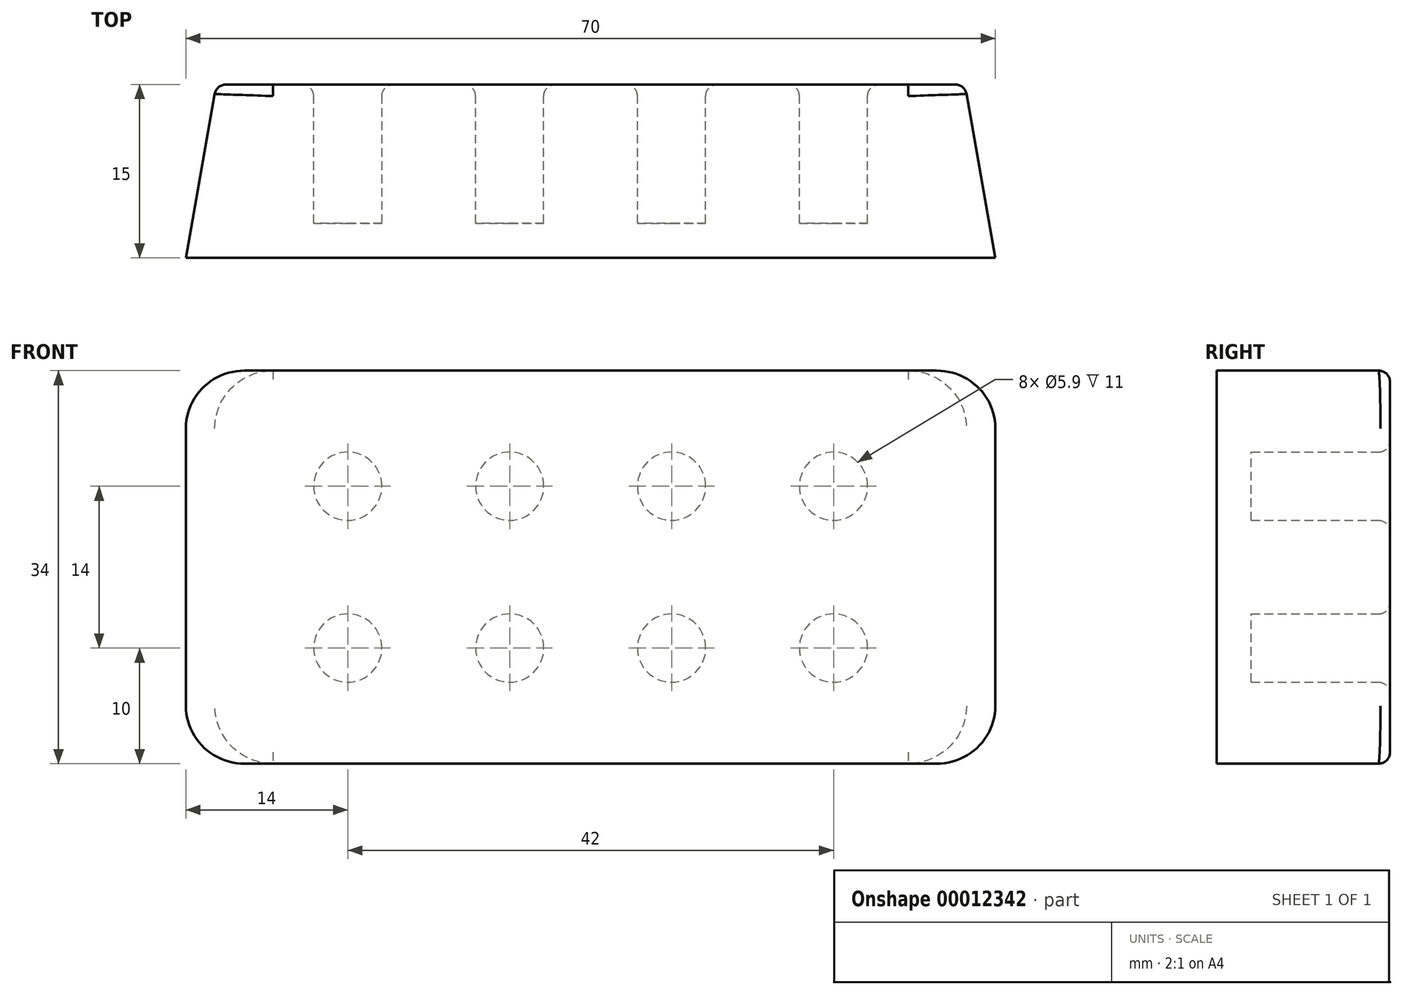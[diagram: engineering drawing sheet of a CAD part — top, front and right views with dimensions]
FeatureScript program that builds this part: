
annotation { "Feature Type Name" : "Feature", "Feature Type Description" : "" }
export const myFeature = defineFeature(function(context is Context, id is Id, definition is map)
    precondition{}
    {
        {
            var Q0;
            Q0=qCreatedBy(makeId("Front.planeOp"),FACE);
            var sketch = newSketch(context, id + "F0", { "sketchPlane" : qUnion([Q0])});
            skLineSegment(sketch, "E0.bottom", {"start": v(0, 0) * mm, "end": v(70, 0) * mm});
            skLineSegment(sketch, "E0.top", {"start": v(0, 34) * mm, "end": v(70, 34) * mm});
            skLineSegment(sketch, "E0.left", {"start": v(0, 0) * mm, "end": v(0, 34) * mm});
            skLineSegment(sketch, "E0.right", {"start": v(70, 0) * mm, "end": v(70, 34) * mm});
            skCircle(sketch, "E1", {"center": v(14, 10) * mm, "radius": 2.95 * mm});
            skCircle(sketch, "E2.0.1.0", {"center": v(14, 24) * mm, "radius": 2.95 * mm});
            skCircle(sketch, "E2.1.0.0", {"center": v(28, 10) * mm, "radius": 2.95 * mm});
            skCircle(sketch, "E2.1.1.0", {"center": v(28, 24) * mm, "radius": 2.95 * mm});
            skCircle(sketch, "E2.2.0.0", {"center": v(42, 10) * mm, "radius": 2.95 * mm});
            skCircle(sketch, "E2.2.1.0", {"center": v(42, 24) * mm, "radius": 2.95 * mm});
            skCircle(sketch, "E2.3.0.0", {"center": v(56, 10) * mm, "radius": 2.95 * mm});
            skCircle(sketch, "E2.3.1.0", {"center": v(56, 24) * mm, "radius": 2.95 * mm});
            skLineSegment(sketch, "E2.direction1", {"start": v(14, 10) * mm, "end": v(28, 10) * mm, "construction": true});
            skLineSegment(sketch, "E2.direction2", {"start": v(14, 10) * mm, "end": v(14, 24) * mm, "construction": true});
            skSolve(sketch);
        }
        {
            var Q0;
            Q0=makeQuery(id+"F0.imprint","IMPRINT",FACE,{"disambiguationData":[TD([[makeQuery(id+"F0.imprint","IMPRINT",EDGE,{"derivedFrom":sQuery(id+"F0.wireOp",EDGE,"E0.bottom")}),1.0]])]});
            extrude(context, id + "F1", {"entities" : qUnion([Q0]), "depth" : 12 * mm});
        }
        {
            var Q0;
            Q0=makeQuery(id+"F1.opExtrude","CAP_FACE",FACE,{"disambiguationData":[OSD([sQuery(id+"F0.wireOp",EDGE,"E0.bottom"),sQuery(id+"F0.wireOp",EDGE,"E0.top"),sQuery(id+"F0.wireOp",EDGE,"E0.left"),sQuery(id+"F0.wireOp",EDGE,"E0.right"),sQuery(id+"F0.wireOp",EDGE,"E1"),sQuery(id+"F0.wireOp",EDGE,"E2.0.1.0"),sQuery(id+"F0.wireOp",EDGE,"E2.1.0.0"),sQuery(id+"F0.wireOp",EDGE,"E2.1.1.0"),sQuery(id+"F0.wireOp",EDGE,"E2.2.0.0"),sQuery(id+"F0.wireOp",EDGE,"E2.2.1.0"),sQuery(id+"F0.wireOp",EDGE,"E2.3.0.0"),sQuery(id+"F0.wireOp",EDGE,"E2.3.1.0")])],"isStart":false});
            var sketch = newSketch(context, id + "F2", { "sketchPlane" : qUnion([Q0])});
            skLineSegment(sketch, "E3.bottom", {"start": v(0, 34) * mm, "end": v(70, 34) * mm});
            skLineSegment(sketch, "E3.top", {"start": v(0, 0) * mm, "end": v(70, 0) * mm});
            skLineSegment(sketch, "E3.left", {"start": v(0, 34) * mm, "end": v(0, 0) * mm});
            skLineSegment(sketch, "E3.right", {"start": v(70, 34) * mm, "end": v(70, 0) * mm});
            skSolve(sketch);
        }
        {
            var Q0;
            Q0 = qSketchRegion(id + "F2", true);
            extrude(context, id + "F3", {"entities" : qUnion([Q0]), "operationType" : NewBodyOperationType.ADD, "depth" : 3 * mm});
        }
        {
            var Q0;
            Q0=makeQuery(id+"F1.opExtrude","CAP_EDGE",EDGE,{"disambiguationData":[OSD([sQuery(id+"F0.wireOp",EDGE,"E0.left")])],"isStart":true});
            var Q1;
            Q1=makeQuery(id+"F1.opExtrude","CAP_EDGE",EDGE,{"disambiguationData":[OSD([sQuery(id+"F0.wireOp",EDGE,"E0.right")])],"isStart":true});
            chamfer(context, id + "F4", {"entities" : qUnion([Q0, Q1]), "chamferType" : ChamferType.OFFSET_ANGLE, "width" : 15 * mm, "oppositeDirection" : true, "angle" : 10 * degree});
        }
        {
            var Q0;
            Q0=makeQuery(id+"F4.opChamfer","BLEND_EDGE",EDGE,{"blendedFrom":[makeQuery(id+"F1.opExtrude","CAP_EDGE",EDGE,{"disambiguationData":[OSD([sQuery(id+"F0.wireOp",EDGE,"E0.left")])],"isStart":true}),makeQuery(id+"F3.boolean.opBoolean","MERGE",FACE,{"derivedFrom":[makeQuery(id+"F1.opExtrude","SWEPT_FACE",FACE,{"disambiguationData":[OSD([sQuery(id+"F0.wireOp",EDGE,"E0.bottom")])]}),makeQuery(id+"F3.opExtrude","SWEPT_FACE",FACE,{"disambiguationData":[OSD([sQuery(id+"F2.wireOp",EDGE,"E3.top")])]})]})],"blendedInto":[makeQuery(id+"F3.boolean.opBoolean","MERGE",FACE,{"derivedFrom":[makeQuery(id+"F1.opExtrude","SWEPT_FACE",FACE,{"disambiguationData":[OSD([sQuery(id+"F0.wireOp",EDGE,"E0.bottom")])]}),makeQuery(id+"F3.opExtrude","SWEPT_FACE",FACE,{"disambiguationData":[OSD([sQuery(id+"F2.wireOp",EDGE,"E3.top")])]})]})]});
            var Q1;
            Q1=makeQuery(id+"F4.opChamfer","BLEND_EDGE",EDGE,{"blendedFrom":[makeQuery(id+"F1.opExtrude","CAP_EDGE",EDGE,{"disambiguationData":[OSD([sQuery(id+"F0.wireOp",EDGE,"E0.left")])],"isStart":true}),makeQuery(id+"F3.boolean.opBoolean","MERGE",FACE,{"derivedFrom":[makeQuery(id+"F1.opExtrude","SWEPT_FACE",FACE,{"disambiguationData":[OSD([sQuery(id+"F0.wireOp",EDGE,"E0.top")])]}),makeQuery(id+"F3.opExtrude","SWEPT_FACE",FACE,{"disambiguationData":[OSD([sQuery(id+"F2.wireOp",EDGE,"E3.bottom")])]})]})],"blendedInto":[makeQuery(id+"F3.boolean.opBoolean","MERGE",FACE,{"derivedFrom":[makeQuery(id+"F1.opExtrude","SWEPT_FACE",FACE,{"disambiguationData":[OSD([sQuery(id+"F0.wireOp",EDGE,"E0.top")])]}),makeQuery(id+"F3.opExtrude","SWEPT_FACE",FACE,{"disambiguationData":[OSD([sQuery(id+"F2.wireOp",EDGE,"E3.bottom")])]})]})]});
            var Q2;
            Q2=makeQuery(id+"F4.opChamfer","BLEND_EDGE",EDGE,{"blendedFrom":[makeQuery(id+"F1.opExtrude","CAP_EDGE",EDGE,{"disambiguationData":[OSD([sQuery(id+"F0.wireOp",EDGE,"E0.right")])],"isStart":true}),makeQuery(id+"F3.boolean.opBoolean","MERGE",FACE,{"derivedFrom":[makeQuery(id+"F1.opExtrude","SWEPT_FACE",FACE,{"disambiguationData":[OSD([sQuery(id+"F0.wireOp",EDGE,"E0.top")])]}),makeQuery(id+"F3.opExtrude","SWEPT_FACE",FACE,{"disambiguationData":[OSD([sQuery(id+"F2.wireOp",EDGE,"E3.bottom")])]})]})],"blendedInto":[makeQuery(id+"F3.boolean.opBoolean","MERGE",FACE,{"derivedFrom":[makeQuery(id+"F1.opExtrude","SWEPT_FACE",FACE,{"disambiguationData":[OSD([sQuery(id+"F0.wireOp",EDGE,"E0.top")])]}),makeQuery(id+"F3.opExtrude","SWEPT_FACE",FACE,{"disambiguationData":[OSD([sQuery(id+"F2.wireOp",EDGE,"E3.bottom")])]})]})]});
            var Q3;
            Q3=makeQuery(id+"F4.opChamfer","BLEND_EDGE",EDGE,{"blendedFrom":[makeQuery(id+"F1.opExtrude","CAP_EDGE",EDGE,{"disambiguationData":[OSD([sQuery(id+"F0.wireOp",EDGE,"E0.right")])],"isStart":true}),makeQuery(id+"F3.boolean.opBoolean","MERGE",FACE,{"derivedFrom":[makeQuery(id+"F1.opExtrude","SWEPT_FACE",FACE,{"disambiguationData":[OSD([sQuery(id+"F0.wireOp",EDGE,"E0.bottom")])]}),makeQuery(id+"F3.opExtrude","SWEPT_FACE",FACE,{"disambiguationData":[OSD([sQuery(id+"F2.wireOp",EDGE,"E3.top")])]})]})],"blendedInto":[makeQuery(id+"F3.boolean.opBoolean","MERGE",FACE,{"derivedFrom":[makeQuery(id+"F1.opExtrude","SWEPT_FACE",FACE,{"disambiguationData":[OSD([sQuery(id+"F0.wireOp",EDGE,"E0.bottom")])]}),makeQuery(id+"F3.opExtrude","SWEPT_FACE",FACE,{"disambiguationData":[OSD([sQuery(id+"F2.wireOp",EDGE,"E3.top")])]})]})]});
            fillet(context, id + "F5", {"entities" : qUnion([Q0, Q1, Q2, Q3]), "radius" : 5 * mm, "tangentPropagation" : true, "allowEdgeOverflow" : false});
        }
        {
            var Q0;
            Q0=makeQuery(id+"F1.opExtrude","CAP_EDGE",EDGE,{"disambiguationData":[OSD([sQuery(id+"F0.wireOp",EDGE,"E1")])],"isStart":true});
            var Q1;
            Q1=makeQuery(id+"F1.opExtrude","CAP_EDGE",EDGE,{"disambiguationData":[OSD([sQuery(id+"F0.wireOp",EDGE,"E2.1.0.0")])],"isStart":true});
            var Q2;
            Q2=makeQuery(id+"F1.opExtrude","CAP_EDGE",EDGE,{"disambiguationData":[OSD([sQuery(id+"F0.wireOp",EDGE,"E2.0.1.0")])],"isStart":true});
            var Q3;
            Q3=makeQuery(id+"F1.opExtrude","CAP_EDGE",EDGE,{"disambiguationData":[OSD([sQuery(id+"F0.wireOp",EDGE,"E2.1.1.0")])],"isStart":true});
            var Q4;
            Q4=makeQuery(id+"F1.opExtrude","CAP_EDGE",EDGE,{"disambiguationData":[OSD([sQuery(id+"F0.wireOp",EDGE,"E2.2.1.0")])],"isStart":true});
            var Q5;
            Q5=makeQuery(id+"F1.opExtrude","CAP_EDGE",EDGE,{"disambiguationData":[OSD([sQuery(id+"F0.wireOp",EDGE,"E2.2.0.0")])],"isStart":true});
            var Q6;
            Q6=makeQuery(id+"F1.opExtrude","CAP_EDGE",EDGE,{"disambiguationData":[OSD([sQuery(id+"F0.wireOp",EDGE,"E2.3.0.0")])],"isStart":true});
            var Q7;
            Q7=makeQuery(id+"F1.opExtrude","CAP_EDGE",EDGE,{"disambiguationData":[OSD([sQuery(id+"F0.wireOp",EDGE,"E2.3.1.0")])],"isStart":true});
            var Q8;
            Q8=makeQuery(id+"F1.opExtrude","CAP_EDGE",EDGE,{"disambiguationData":[OSD([sQuery(id+"F0.wireOp",EDGE,"E0.top")])],"isStart":true});
            fillet(context, id + "F6", {"entities" : qUnion([Q0, Q1, Q2, Q3, Q4, Q5, Q6, Q7, Q8]), "radius" : 1 * mm, "tangentPropagation" : true, "allowEdgeOverflow" : false});
        }
    });
